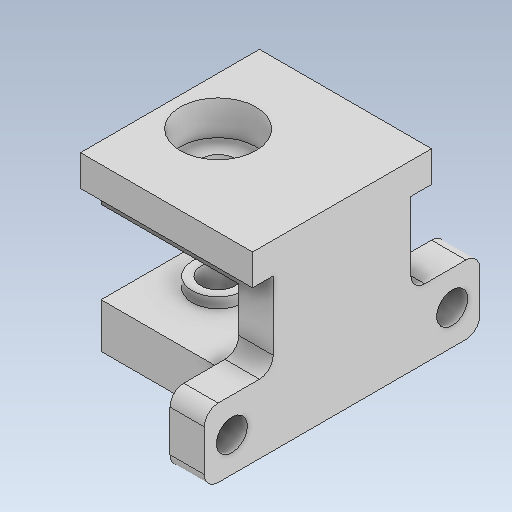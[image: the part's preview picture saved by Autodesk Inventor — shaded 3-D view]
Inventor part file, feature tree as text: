
AUTODESK INVENTOR PART (.ipt)
format: ipt  version: 2020 (Build 240168000, 168)  size: 240,128 bytes
history: native  units: mm
features: sketch x8, extrude x7, hole x2, direct_edit x1, fillet x1, move_body x1
ambient origin geometry x8: Origin, YZ Plane, XZ Plane, XY Plane, X Axis, Y Axis, Z Axis, Center Point
bodies: Solid1 (feature_tree)
feature tree (20):
  extrude  "Extrusion1"  Depth=25.0mm
  extrude  "Extrusion2"  Depth=12.0mm
  hole  "Hole1"  [1 undecoded]
  extrude  "Extrusion3"  Depth=3.0mm
  extrude  "Extrusion5"  Depth=3.0mm
  extrude  "Extrusion4"  Depth=10.0mm
  extrude  "Extrusion6"  Depth=4.5mm
  extrude  "Extrusion7"  Depth=8.0mm
  direct_edit  "Direct Edit2"
  fillet  "Fillet2"  Radius=4.0mm
  hole  "Hole3"  [1 undecoded]
  sketch  "Sketch1"  dims[d0=25.0mm d1=25.0mm]
  sketch  "Sketch2"  dims[d2=20.0mm d3=0.0mm d4=12.0mm]
  sketch  "Sketch3"  dims[d5=5.0mm d6=0.0mm d7=0.0mm]
  sketch  "Sketch4"  dims[d8=7.0mm]
  sketch  "Sketch6"  dims[d9=5.0mm d10=6.0mm d11=4.0mm d12=2.0mm d13=90.0deg d14=2.0mm d15=20.594885mm d16=3.0mm]
  sketch  "Sketch8"  dims[d17=3.0mm d18=0.0mm d26=3.0mm]
  sketch  "Sketch9"  dims[d27=2.0mm d28=0.0mm d30=10.0mm]
  sketch  "Sketch11"  dims[d31=10.0mm d32=4.5mm d33=4.0mm d34=4.0mm d35=0.0mm d36=0.0mm d37=7.5mm d38=10.0mm d39=0.0mm d40=1.5mm d41=1.5mm d42=0.0mm d43=0.0mm d47=0.0mm d48=0.0mm d49=1.5mm d50=10.0mm d51=0.0mm d53=2.0mm d55=5.0mm d56=6.0mm d57=11.0mm d58=5.0mm d59=90.0deg d60=8.0mm d61=20.594885mm]
  move_body  "Move2"
note: 2 required parameter values undecoded (feature->parameter linkage not recoverable at this tier; creation-order binding heuristic only, values carry confidence <= 0.55)
